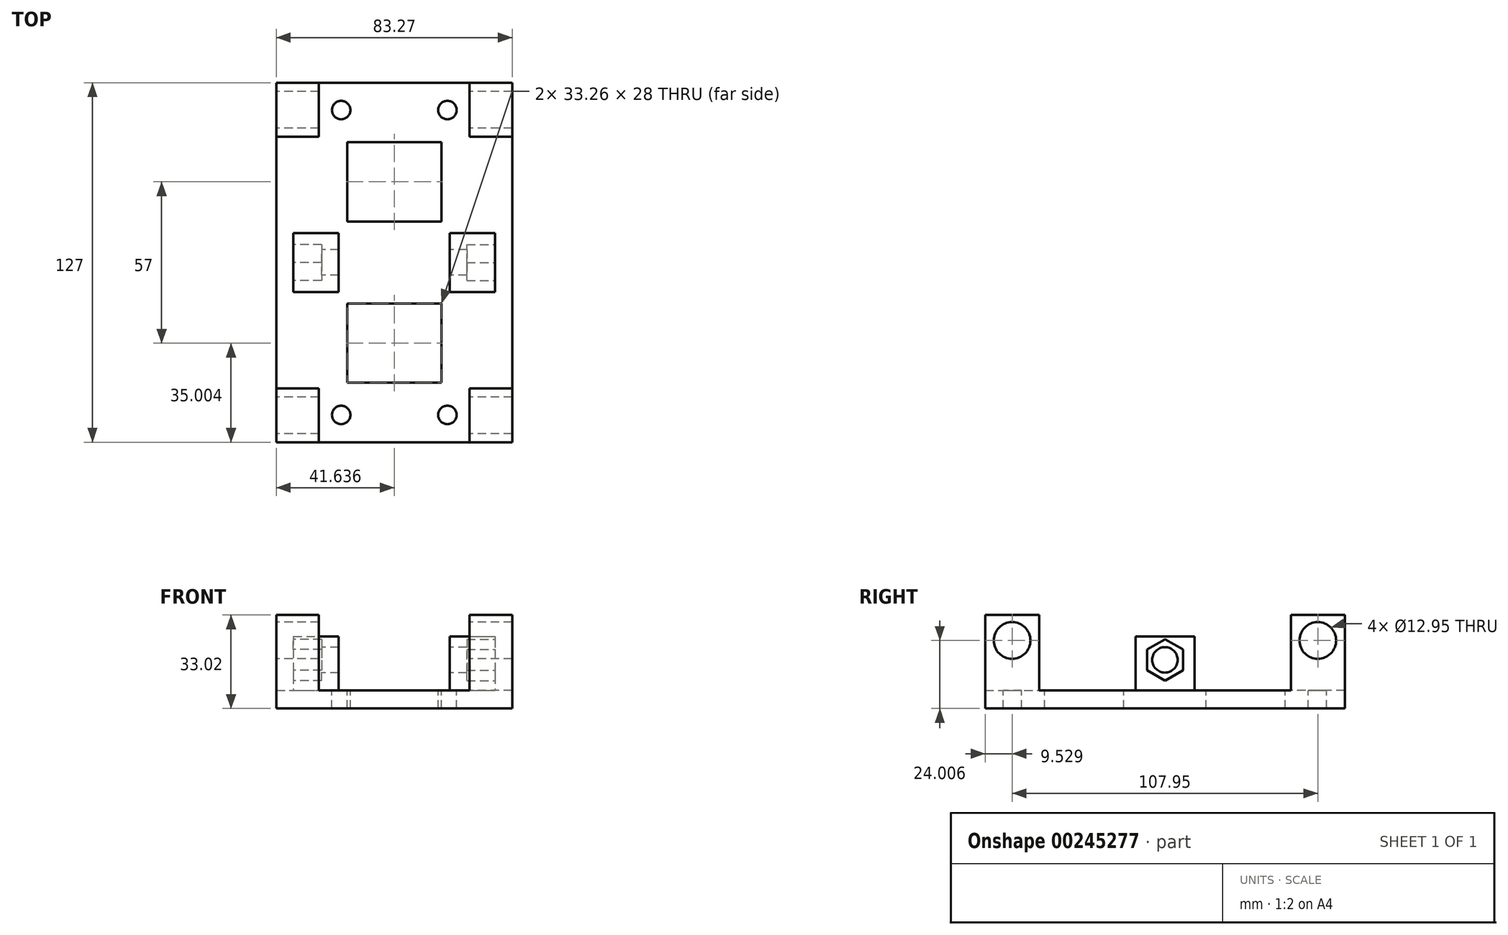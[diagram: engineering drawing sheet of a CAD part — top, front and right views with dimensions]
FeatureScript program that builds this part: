
annotation { "Feature Type Name" : "Feature", "Feature Type Description" : "" }
export const myFeature = defineFeature(function(context is Context, id is Id, definition is map)
    precondition{}
    {
        {
            var Q0;
            Q0=qCreatedBy(makeId("Top.planeOp"),FACE);
            var sketch = newSketch(context, id + "F0", { "sketchPlane" : qUnion([Q0])});
            skLineSegment(sketch, "E0.bottom", {"start": v(-45.28, 64.7) * mm, "end": v(37.99, 64.7) * mm});
            skLineSegment(sketch, "E0.top", {"start": v(-45.28, -62.3) * mm, "end": v(37.99, -62.3) * mm});
            skLineSegment(sketch, "E0.left", {"start": v(-45.28, 64.7) * mm, "end": v(-45.28, -62.3) * mm});
            skLineSegment(sketch, "E0.right", {"start": v(37.99, 64.7) * mm, "end": v(37.99, -62.3) * mm});
            skSolve(sketch);
        }
        {
            var Q0;
            Q0=makeQuery(id+"F0.imprint","IMPRINT",FACE,{"disambiguationData":[TD([[makeQuery(id+"F0.imprint","IMPRINT",EDGE,{"derivedFrom":sQuery(id+"F0.wireOp",EDGE,"E0.bottom")}),-1.0]])]});
            extrude(context, id + "F1", {"entities" : qUnion([Q0]), "depth" : 6.35 * mm});
        }
        {
            var Q0;
            Q0=makeQuery(id+"F1.opExtrude","CAP_FACE",FACE,{"disambiguationData":[OSD([sQuery(id+"F0.wireOp",EDGE,"E0.bottom"),sQuery(id+"F0.wireOp",EDGE,"E0.top"),sQuery(id+"F0.wireOp",EDGE,"E0.left"),sQuery(id+"F0.wireOp",EDGE,"E0.right")])],"isStart":false});
            var sketch = newSketch(context, id + "F2", { "sketchPlane" : qUnion([Q0])});
            skLineSegment(sketch, "E1.bottom", {"start": v(-45.28, 64.7) * mm, "end": v(-30.28, 64.7) * mm});
            skLineSegment(sketch, "E1.top", {"start": v(-45.28, 45.64) * mm, "end": v(-30.28, 45.64) * mm});
            skLineSegment(sketch, "E1.left", {"start": v(-45.28, 64.7) * mm, "end": v(-45.28, 45.64) * mm});
            skLineSegment(sketch, "E1.right", {"start": v(-30.28, 64.7) * mm, "end": v(-30.28, 45.64) * mm});
            skLineSegment(sketch, "E2.bottom", {"start": v(37.99, 64.7) * mm, "end": v(22.99, 64.7) * mm});
            skLineSegment(sketch, "E2.top", {"start": v(37.99, 45.64) * mm, "end": v(22.99, 45.64) * mm});
            skLineSegment(sketch, "E2.left", {"start": v(37.99, 64.7) * mm, "end": v(37.99, 45.64) * mm});
            skLineSegment(sketch, "E2.right", {"start": v(22.99, 64.7) * mm, "end": v(22.99, 45.64) * mm});
            skLineSegment(sketch, "E3.bottom", {"start": v(37.99, -62.3) * mm, "end": v(22.99, -62.3) * mm});
            skLineSegment(sketch, "E3.top", {"start": v(37.99, -43.26) * mm, "end": v(22.99, -43.26) * mm});
            skLineSegment(sketch, "E3.left", {"start": v(37.99, -62.3) * mm, "end": v(37.99, -43.26) * mm});
            skLineSegment(sketch, "E3.right", {"start": v(22.99, -62.3) * mm, "end": v(22.99, -43.26) * mm});
            skLineSegment(sketch, "E4.bottom", {"start": v(-45.28, -62.3) * mm, "end": v(-30.28, -62.3) * mm});
            skLineSegment(sketch, "E4.top", {"start": v(-45.28, -43.26) * mm, "end": v(-30.28, -43.26) * mm});
            skLineSegment(sketch, "E4.left", {"start": v(-45.28, -62.3) * mm, "end": v(-45.28, -43.26) * mm});
            skLineSegment(sketch, "E4.right", {"start": v(-30.28, -62.3) * mm, "end": v(-30.28, -43.26) * mm});
            skSolve(sketch);
        }
        {
            var Q0;
            Q0 = qSketchRegion(id + "F2", true);
            extrude(context, id + "F3", {"entities" : qUnion([Q0]), "operationType" : NewBodyOperationType.ADD, "depth" : 26.67 * mm});
        }
        {
            var Q0;
            Q0=makeQuery(id+"F3.boolean.opBoolean","MERGE",FACE,{"derivedFrom":[makeQuery(id+"F1.opExtrude","SWEPT_FACE",FACE,{"disambiguationData":[OSD([sQuery(id+"F0.wireOp",EDGE,"E0.left")])]}),makeQuery(id+"F3.opExtrude","SWEPT_FACE",FACE,{"disambiguationData":[OSD([sQuery(id+"F2.wireOp",EDGE,"E1.left")])]}),makeQuery(id+"F3.opExtrude","SWEPT_FACE",FACE,{"disambiguationData":[OSD([sQuery(id+"F2.wireOp",EDGE,"E4.left")])]})]});
            var sketch = newSketch(context, id + "F4", { "sketchPlane" : qUnion([Q0])});
            skPoint(sketch, "E5", {"position": v(52.78, 24) * mm});
            skPoint(sketch, "E6", {"position": v(-55.17, 24) * mm});
            skSolve(sketch);
        }
        {
            var Q0;
            Q0=sQuery(id+"F4.wireOp",VERTEX,"E6");
            var Q1;
            Q1=sQuery(id+"F4.wireOp",VERTEX,"E5");
            var Q2;
            Q2=makeQuery(id+"F1.opExtrude","SWEPT_BODY",BODY,{"disambiguationData":[OSD([sQuery(id+"F0.wireOp",EDGE,"E0.bottom"),sQuery(id+"F0.wireOp",EDGE,"E0.top"),sQuery(id+"F0.wireOp",EDGE,"E0.left"),sQuery(id+"F0.wireOp",EDGE,"E0.right")])]});
            hole(context, id + "F5", {"style" : HoleStyle.SIMPLE, "endStyle" : HoleEndStyle.THROUGH, "holeDiameter" : 12.95 * mm, "tappedDepth" : 12 * mm, "tapClearance" : 3, "locations" : qUnion([Q0, Q1]), "scope" : qUnion([Q2])});
        }
        {
            var Q0;
            Q0=makeQuery(id+"F1.opExtrude","CAP_FACE",FACE,{"disambiguationData":[OSD([sQuery(id+"F0.wireOp",EDGE,"E0.bottom"),sQuery(id+"F0.wireOp",EDGE,"E0.top"),sQuery(id+"F0.wireOp",EDGE,"E0.left"),sQuery(id+"F0.wireOp",EDGE,"E0.right")])],"isStart":false});
            var sketch = newSketch(context, id + "F6", { "sketchPlane" : qUnion([Q0])});
            skPoint(sketch, "E7", {"position": v(-22.4, 55.04) * mm});
            skPoint(sketch, "E8", {"position": v(15.11, 55.04) * mm});
            skPoint(sketch, "E9", {"position": v(-22.4, -52.65) * mm});
            skPoint(sketch, "E10", {"position": v(15.11, -52.65) * mm});
            skSolve(sketch);
        }
        {
            var Q0;
            Q0=sQuery(id+"F6.wireOp",VERTEX,"E7");
            var Q1;
            Q1=sQuery(id+"F6.wireOp",VERTEX,"E8");
            var Q2;
            Q2=sQuery(id+"F6.wireOp",VERTEX,"93de815d-9985-434b-9f85-75e5ad459bd7");
            var Q3;
            Q3=sQuery(id+"F6.wireOp",VERTEX,"44c02424-169e-4457-9cc6-0524908b7b72");
            var Q4;
            Q4=sQuery(id+"F6.wireOp",VERTEX,"E9");
            var Q5;
            Q5=sQuery(id+"F6.wireOp",VERTEX,"E10");
            var Q6;
            Q6=sQuery(id+"F6.wireOp",VERTEX,"78eef1c9-758d-4e63-b6ed-ccdf94f1ce2f");
            var Q7;
            Q7=sQuery(id+"F6.wireOp",VERTEX,"7332527d-e9d9-4fb1-8077-11bcb0172503");
            var Q8;
            Q8=makeQuery(id+"F1.opExtrude","SWEPT_BODY",BODY,{"disambiguationData":[OSD([sQuery(id+"F0.wireOp",EDGE,"E0.bottom"),sQuery(id+"F0.wireOp",EDGE,"E0.top"),sQuery(id+"F0.wireOp",EDGE,"E0.left"),sQuery(id+"F0.wireOp",EDGE,"E0.right")])]});
            hole(context, id + "F7", {"style" : HoleStyle.SIMPLE, "endStyle" : HoleEndStyle.THROUGH, "holeDiameter" : 6.53 * mm, "tappedDepth" : 12 * mm, "tapClearance" : 3, "locations" : qUnion([Q0, Q1, Q2, Q3, Q4, Q5, Q6, Q7]), "scope" : qUnion([Q8])});
        }
        {
            var Q0;
            Q0=makeQuery(id+"F1.opExtrude","CAP_FACE",FACE,{"disambiguationData":[OSD([sQuery(id+"F0.wireOp",EDGE,"E0.bottom"),sQuery(id+"F0.wireOp",EDGE,"E0.top"),sQuery(id+"F0.wireOp",EDGE,"E0.left"),sQuery(id+"F0.wireOp",EDGE,"E0.right")])],"isStart":false});
            var sketch = newSketch(context, id + "F8", { "sketchPlane" : qUnion([Q0])});
            skLineSegment(sketch, "E11.bottom", {"start": v(-39.28, 11.6) * mm, "end": v(-23.28, 11.6) * mm});
            skLineSegment(sketch, "E11.top", {"start": v(-39.28, -9.22) * mm, "end": v(-23.28, -9.22) * mm});
            skLineSegment(sketch, "E11.left", {"start": v(-39.28, 11.6) * mm, "end": v(-39.28, -9.22) * mm});
            skLineSegment(sketch, "E11.right", {"start": v(-23.28, 11.6) * mm, "end": v(-23.28, -9.22) * mm});
            skLineSegment(sketch, "E12.bottom", {"start": v(15.99, 11.6) * mm, "end": v(31.99, 11.6) * mm});
            skLineSegment(sketch, "E12.top", {"start": v(15.99, -9.22) * mm, "end": v(31.99, -9.22) * mm});
            skLineSegment(sketch, "E12.left", {"start": v(15.99, 11.6) * mm, "end": v(15.99, -9.22) * mm});
            skLineSegment(sketch, "E12.right", {"start": v(31.99, 11.6) * mm, "end": v(31.99, -9.22) * mm});
            skSolve(sketch);
        }
        {
            var Q0;
            Q0 = qSketchRegion(id + "F8", true);
            extrude(context, id + "F9", {"entities" : qUnion([Q0]), "operationType" : NewBodyOperationType.ADD, "depth" : 19.05 * mm});
        }
        {
            var Q0;
            Q0=makeQuery(id+"F9.opExtrude","SWEPT_FACE",FACE,{"disambiguationData":[OSD([sQuery(id+"F8.wireOp",EDGE,"E11.left")])]});
            var sketch = newSketch(context, id + "F10", { "sketchPlane" : qUnion([Q0])});
            skCircle(sketch, "E13.cCircle", {"center": v(-1.2, 17.14) * mm, "radius": 6.34 * mm, "construction": true});
            skLineSegment(sketch, "E13.0", {"start": v(5.15, 20.8) * mm, "end": v(5.15, 13.48) * mm});
            skLineSegment(sketch, "E13.1", {"start": v(5.15, 13.48) * mm, "end": v(-1.2, 9.82) * mm});
            skLineSegment(sketch, "E13.2", {"start": v(-1.2, 9.82) * mm, "end": v(-7.53, 13.48) * mm});
            skLineSegment(sketch, "E13.3", {"start": v(-7.53, 13.48) * mm, "end": v(-7.53, 20.8) * mm});
            skLineSegment(sketch, "E13.4", {"start": v(-7.53, 20.8) * mm, "end": v(-1.2, 24.47) * mm});
            skLineSegment(sketch, "E13.5", {"start": v(-1.2, 24.47) * mm, "end": v(5.15, 20.8) * mm});
            skPoint(sketch, "E13.0.midPoint", {"position": v(5.15, 17.14) * mm});
            skSolve(sketch);
        }
        {
            var Q0;
            Q0=makeQuery(id+"F10.imprint","IMPRINT",FACE,{"disambiguationData":[TD([[makeQuery(id+"F10.imprint","IMPRINT",EDGE,{"derivedFrom":sQuery(id+"F10.wireOp",EDGE,"E13.0")}),-1.0]])]});
            extrude(context, id + "F11", {"entities" : qUnion([Q0]), "operationType" : NewBodyOperationType.REMOVE, "oppositeDirection" : true, "depth" : 10 * mm});
        }
        {
            var Q0;
            Q0=makeQuery(id+"F9.opExtrude","SWEPT_FACE",FACE,{"disambiguationData":[OSD([sQuery(id+"F8.wireOp",EDGE,"E12.right")])]});
            var sketch = newSketch(context, id + "F12", { "sketchPlane" : qUnion([Q0])});
            skCircle(sketch, "E14.cCircle", {"center": v(1.2, 17.14) * mm, "radius": 6.34 * mm, "construction": true});
            skLineSegment(sketch, "E14.0", {"start": v(7.53, 20.8) * mm, "end": v(7.53, 13.48) * mm});
            skLineSegment(sketch, "E14.1", {"start": v(7.53, 13.48) * mm, "end": v(1.2, 9.82) * mm});
            skLineSegment(sketch, "E14.2", {"start": v(1.2, 9.82) * mm, "end": v(-5.15, 13.48) * mm});
            skLineSegment(sketch, "E14.3", {"start": v(-5.15, 13.48) * mm, "end": v(-5.15, 20.8) * mm});
            skLineSegment(sketch, "E14.4", {"start": v(-5.15, 20.8) * mm, "end": v(1.2, 24.47) * mm});
            skLineSegment(sketch, "E14.5", {"start": v(1.2, 24.47) * mm, "end": v(7.53, 20.8) * mm});
            skPoint(sketch, "E14.0.midPoint", {"position": v(7.53, 17.14) * mm});
            skSolve(sketch);
        }
        {
            var Q0;
            Q0 = qSketchRegion(id + "F12", true);
            extrude(context, id + "F13", {"entities" : qUnion([Q0]), "operationType" : NewBodyOperationType.REMOVE, "oppositeDirection" : true, "depth" : 10 * mm});
        }
        {
            var Q0;
            Q0=makeQuery(id+"F11.boolean.opBoolean","COPY",FACE,{"derivedFrom":makeQuery(id+"F11.opExtrude","CAP_FACE",FACE,{"disambiguationData":[OSD([sQuery(id+"F10.wireOp",EDGE,"E13.0"),sQuery(id+"F10.wireOp",EDGE,"E13.1"),sQuery(id+"F10.wireOp",EDGE,"E13.2"),sQuery(id+"F10.wireOp",EDGE,"E13.3"),sQuery(id+"F10.wireOp",EDGE,"E13.4"),sQuery(id+"F10.wireOp",EDGE,"E13.5")])],"isStart":false})});
            var sketch = newSketch(context, id + "F14", { "sketchPlane" : qUnion([Q0])});
            skPoint(sketch, "E15", {"position": v(-1.2, 17.14) * mm});
            skSolve(sketch);
        }
        {
            var Q0;
            Q0=sQuery(id+"F14.wireOp",VERTEX,"E15");
            var Q1;
            Q1=makeQuery(id+"F1.opExtrude","SWEPT_BODY",BODY,{"disambiguationData":[OSD([sQuery(id+"F0.wireOp",EDGE,"E0.bottom"),sQuery(id+"F0.wireOp",EDGE,"E0.top"),sQuery(id+"F0.wireOp",EDGE,"E0.left"),sQuery(id+"F0.wireOp",EDGE,"E0.right")])]});
            hole(context, id + "F15", {"style" : HoleStyle.SIMPLE, "endStyle" : HoleEndStyle.THROUGH, "holeDiameter" : 9 * mm, "tappedDepth" : 12 * mm, "tapClearance" : 3, "locations" : qUnion([Q0]), "scope" : qUnion([Q1])});
        }
        {
            var Q0;
            Q0=makeQuery(id+"F1.opExtrude","CAP_FACE",FACE,{"disambiguationData":[OSD([sQuery(id+"F0.wireOp",EDGE,"E0.bottom"),sQuery(id+"F0.wireOp",EDGE,"E0.top"),sQuery(id+"F0.wireOp",EDGE,"E0.left"),sQuery(id+"F0.wireOp",EDGE,"E0.right")])],"isStart":false});
            var sketch = newSketch(context, id + "F16", { "sketchPlane" : qUnion([Q0])});
            skLineSegment(sketch, "E16.bottom", {"start": v(-20.28, 43.7) * mm, "end": v(12.99, 43.7) * mm});
            skLineSegment(sketch, "E16.top", {"start": v(-20.28, 15.7) * mm, "end": v(12.99, 15.7) * mm});
            skLineSegment(sketch, "E16.left", {"start": v(-20.28, 43.7) * mm, "end": v(-20.28, 15.7) * mm});
            skLineSegment(sketch, "E16.right", {"start": v(12.99, 43.7) * mm, "end": v(12.99, 15.7) * mm});
            skLineSegment(sketch, "E17.bottom", {"start": v(-20.28, -13.3) * mm, "end": v(12.99, -13.3) * mm});
            skLineSegment(sketch, "E17.top", {"start": v(-20.28, -41.3) * mm, "end": v(12.99, -41.3) * mm});
            skLineSegment(sketch, "E17.left", {"start": v(-20.28, -13.3) * mm, "end": v(-20.28, -41.3) * mm});
            skLineSegment(sketch, "E17.right", {"start": v(12.99, -13.3) * mm, "end": v(12.99, -41.3) * mm});
            skSolve(sketch);
        }
        {
            var Q0;
            Q0 = qSketchRegion(id + "F16", true);
            extrude(context, id + "F17", {"entities" : qUnion([Q0]), "operationType" : NewBodyOperationType.REMOVE, "endBound" : BoundingType.THROUGH_ALL, "oppositeDirection" : true, "depth" : 25 * mm});
        }
    });
